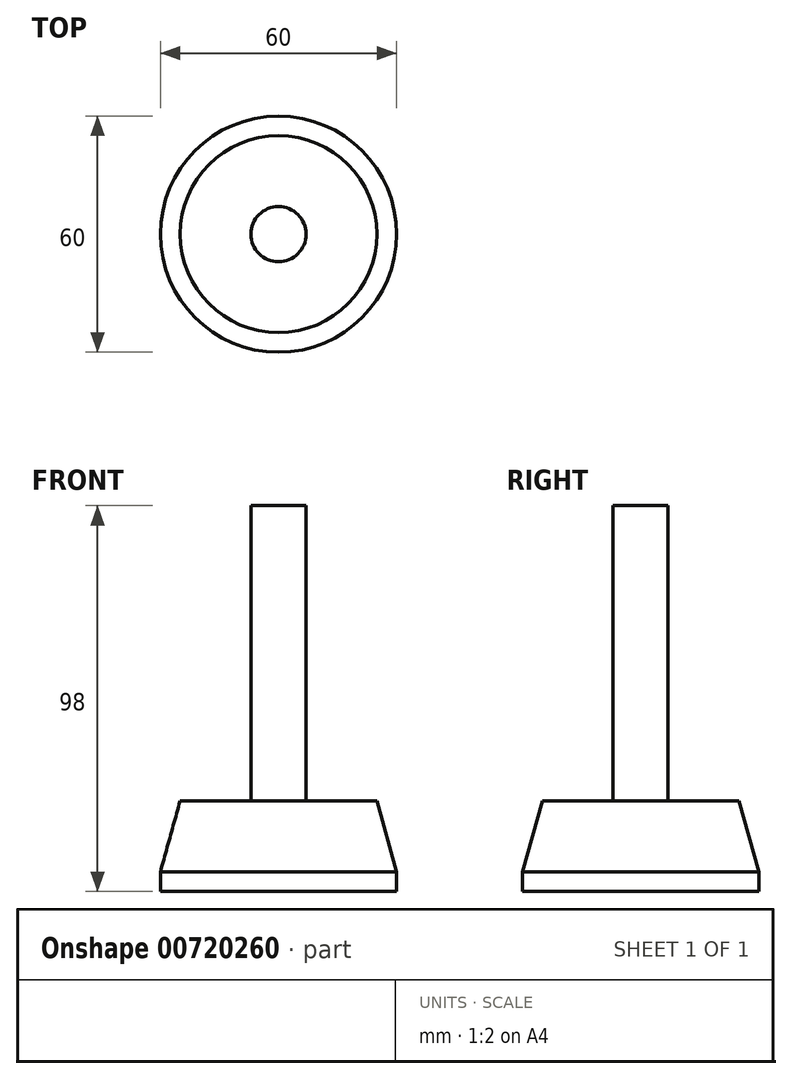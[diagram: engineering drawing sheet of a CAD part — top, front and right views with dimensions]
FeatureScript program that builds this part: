
annotation { "Feature Type Name" : "Feature", "Feature Type Description" : "" }
export const myFeature = defineFeature(function(context is Context, id is Id, definition is map)
    precondition{}
    {
        {
            var Q0;
            Q0=qCreatedBy(makeId("Front.planeOp"),FACE);
            var sketch = newSketch(context, id + "F0", { "sketchPlane" : qUnion([Q0])});
            skLineSegment(sketch, "E0", {"start": v(0, 0) * mm, "end": v(30, 0) * mm});
            skLineSegment(sketch, "E1", {"start": v(30, 0) * mm, "end": v(30, 5) * mm});
            skLineSegment(sketch, "E2", {"start": v(0, 23) * mm, "end": v(25, 23) * mm});
            skLineSegment(sketch, "E3", {"start": v(25, 23) * mm, "end": v(30, 5) * mm});
            skLineSegment(sketch, "E4", {"start": v(7, 23) * mm, "end": v(7, 98) * mm});
            skLineSegment(sketch, "E5", {"start": v(7, 98) * mm, "end": v(0, 98) * mm});
            skLineSegment(sketch, "E6", {"start": v(0, 0) * mm, "end": v(0, 98) * mm});
            skSolve(sketch);
        }
        {
            var Q0;
            Q0 = qSketchRegion(id + "F0", true);
            var Q1;
            Q1=sQuery(id+"F0.wireOp",EDGE,"E6");
            revolve(context, id + "F1", {"surfaceOperationType" : NewSurfaceOperationType.NEW, "entities" : qUnion([Q0]), "axis" : qUnion([Q1]), "revolveType" : RevolveType.FULL});
        }
    });
